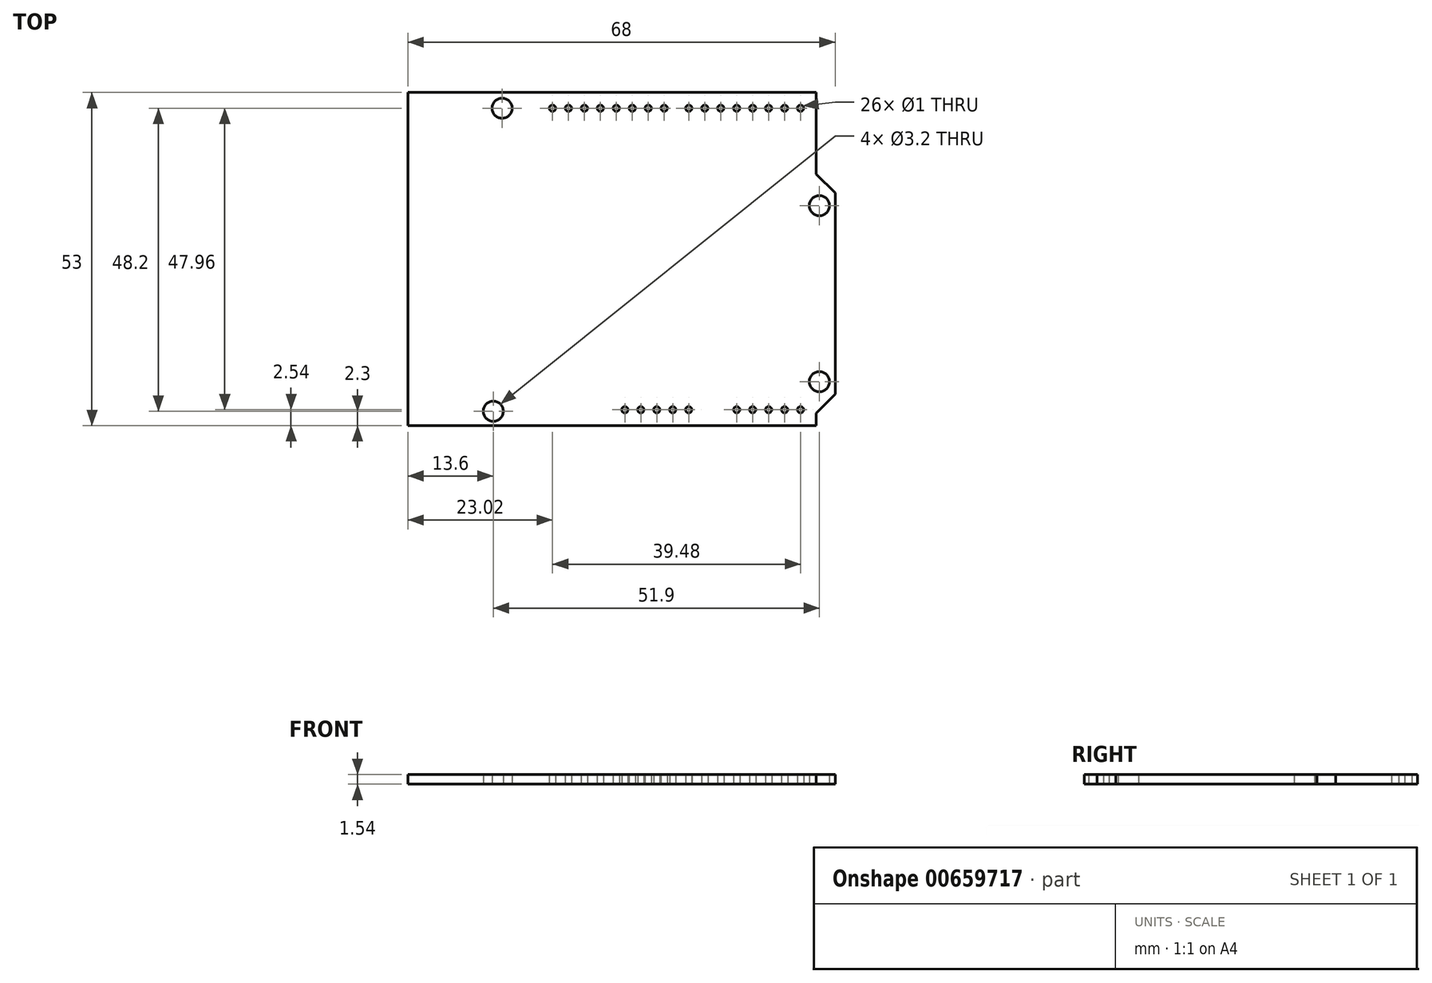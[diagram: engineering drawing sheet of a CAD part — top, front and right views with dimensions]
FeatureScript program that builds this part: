
annotation { "Feature Type Name" : "Feature", "Feature Type Description" : "" }
export const myFeature = defineFeature(function(context is Context, id is Id, definition is map)
    precondition{}
    {
        {
            var Q0;
            Q0=qCreatedBy(makeId("Top.planeOp"),FACE);
            var sketch = newSketch(context, id + "F0", { "sketchPlane" : qUnion([Q0])});
            skLineSegment(sketch, "E0.bottom", {"start": v(0, 0) * mm, "end": v(68, 0) * mm});
            skLineSegment(sketch, "E0.top", {"start": v(0, 53) * mm, "end": v(68, 53) * mm});
            skLineSegment(sketch, "E0.left", {"start": v(0, 0) * mm, "end": v(0, 53) * mm});
            skLineSegment(sketch, "E0.right", {"start": v(68, 0) * mm, "end": v(68, 53) * mm});
            skCircle(sketch, "E1", {"center": v(15, 50.5) * mm, "radius": 1.6 * mm});
            skCircle(sketch, "E2", {"center": v(65.5, 35) * mm, "radius": 1.6 * mm});
            skCircle(sketch, "E3", {"center": v(65.5, 7) * mm, "radius": 1.6 * mm});
            skLineSegment(sketch, "E4", {"start": v(65, 0) * mm, "end": v(65, 2) * mm});
            skLineSegment(sketch, "E5", {"start": v(65, 2) * mm, "end": v(68, 5) * mm});
            skLineSegment(sketch, "E6", {"start": v(65, 53) * mm, "end": v(65, 40) * mm});
            skLineSegment(sketch, "E7", {"start": v(65, 40) * mm, "end": v(68, 37) * mm});
            skCircle(sketch, "E8", {"center": v(13.6, 2.3) * mm, "radius": 1.6 * mm});
            skCircle(sketch, "E9", {"center": v(62.5, 2.54) * mm, "radius": 0.5 * mm});
            skCircle(sketch, "E10", {"center": v(59.96, 2.54) * mm, "radius": 0.5 * mm});
            skCircle(sketch, "E11", {"center": v(57.42, 2.54) * mm, "radius": 0.5 * mm});
            skCircle(sketch, "E12", {"center": v(54.88, 2.54) * mm, "radius": 0.5 * mm});
            skCircle(sketch, "E13", {"center": v(52.34, 2.54) * mm, "radius": 0.5 * mm});
            skCircle(sketch, "E14", {"center": v(44.7, 2.54) * mm, "radius": 0.5 * mm});
            skCircle(sketch, "E15", {"center": v(42.16, 2.54) * mm, "radius": 0.5 * mm});
            skCircle(sketch, "E16", {"center": v(39.62, 2.54) * mm, "radius": 0.5 * mm});
            skCircle(sketch, "E17", {"center": v(37.08, 2.54) * mm, "radius": 0.5 * mm});
            skCircle(sketch, "E18", {"center": v(34.54, 2.54) * mm, "radius": 0.5 * mm});
            skCircle(sketch, "E19", {"center": v(62.5, 50.5) * mm, "radius": 0.5 * mm});
            skCircle(sketch, "E20", {"center": v(59.96, 50.5) * mm, "radius": 0.5 * mm});
            skCircle(sketch, "E21", {"center": v(57.42, 50.5) * mm, "radius": 0.5 * mm});
            skCircle(sketch, "E22", {"center": v(54.88, 50.5) * mm, "radius": 0.5 * mm});
            skCircle(sketch, "E23", {"center": v(52.34, 50.5) * mm, "radius": 0.5 * mm});
            skCircle(sketch, "E24", {"center": v(40.8, 50.5) * mm, "radius": 0.5 * mm});
            skCircle(sketch, "E25", {"center": v(38.26, 50.5) * mm, "radius": 0.5 * mm});
            skCircle(sketch, "E26", {"center": v(35.72, 50.5) * mm, "radius": 0.5 * mm});
            skCircle(sketch, "E27", {"center": v(33.18, 50.5) * mm, "radius": 0.5 * mm});
            skCircle(sketch, "E28", {"center": v(30.64, 50.5) * mm, "radius": 0.5 * mm});
            skCircle(sketch, "E29", {"center": v(28.1, 50.5) * mm, "radius": 0.5 * mm});
            skCircle(sketch, "E30", {"center": v(25.56, 50.5) * mm, "radius": 0.5 * mm});
            skCircle(sketch, "E31", {"center": v(23.02, 50.5) * mm, "radius": 0.5 * mm});
            skCircle(sketch, "E32", {"center": v(49.8, 50.5) * mm, "radius": 0.5 * mm});
            skCircle(sketch, "E33", {"center": v(47.26, 50.5) * mm, "radius": 0.5 * mm});
            skCircle(sketch, "E34", {"center": v(44.72, 50.5) * mm, "radius": 0.5 * mm});
            skSolve(sketch);
        }
        {
            var Q0;
            {var subQ3=sQuery(id+"F0.wireOp",EDGE,"E0.left");Q0=makeQuery(id+"F0.imprint","IMPRINT",FACE,{"disambiguationData":[TD([[makeQuery(id+"F0.imprint","IMPRINT",EDGE,{"derivedFrom":subQ3}),-1.0]])]});}
            extrude(context, id + "F1", {"entities" : qUnion([Q0]), "depth" : 1.54 * mm, "offsetDistance" : 25 * mm});
        }
    });
